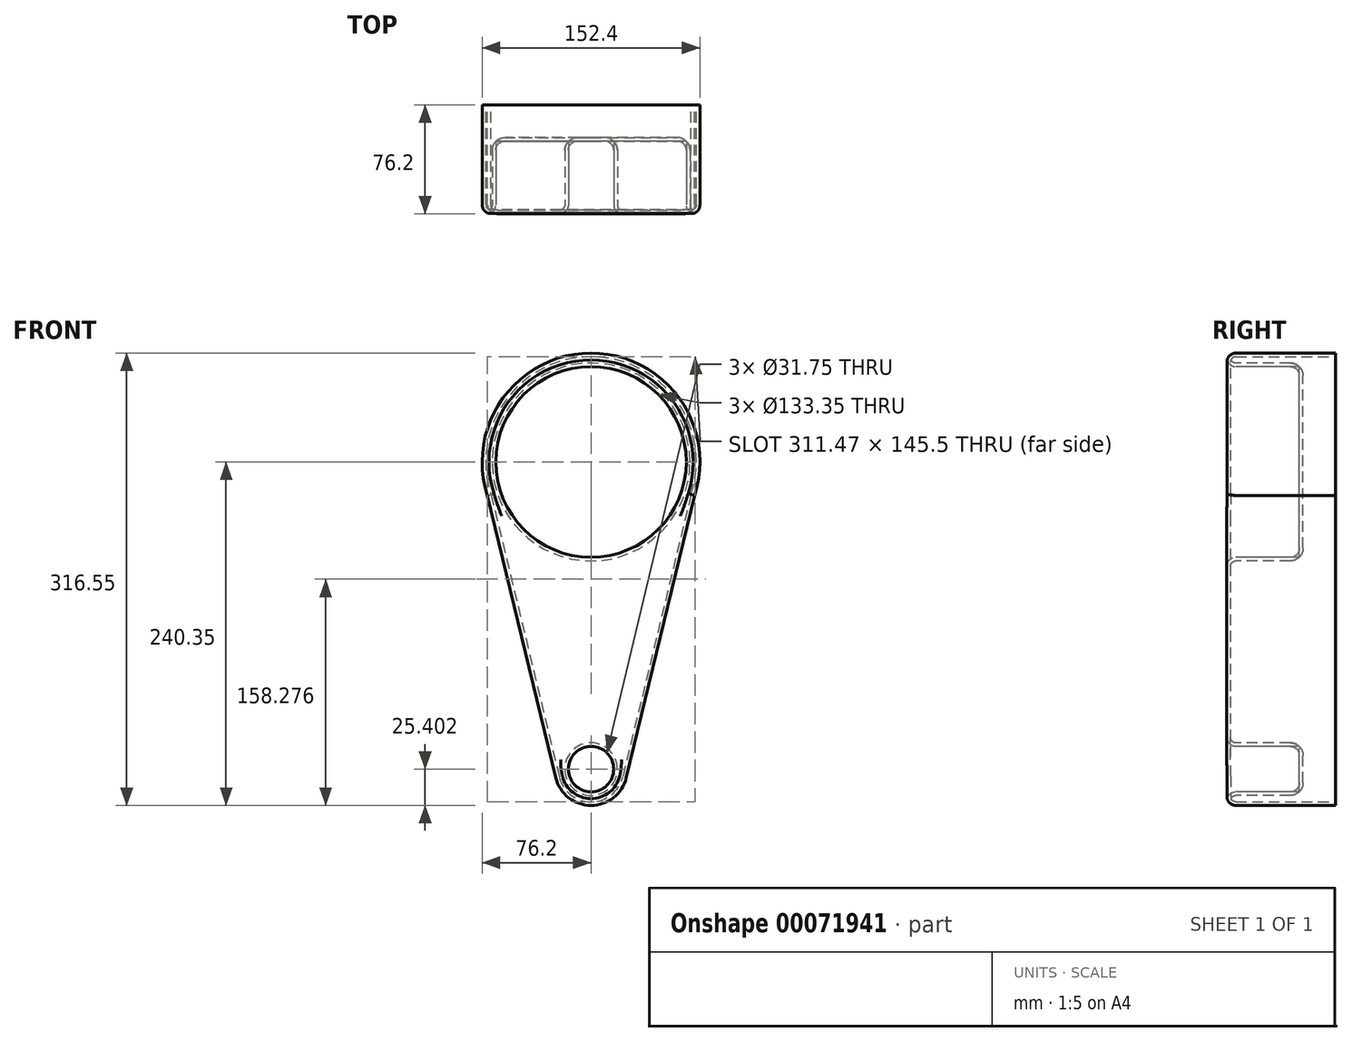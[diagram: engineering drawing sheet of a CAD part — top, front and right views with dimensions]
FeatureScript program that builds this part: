
annotation { "Feature Type Name" : "Feature", "Feature Type Description" : "" }
export const myFeature = defineFeature(function(context is Context, id is Id, definition is map)
    precondition{}
    {
        {
            var Q0;
            Q0=qCreatedBy(makeId("Front.planeOp"),FACE);
            var sketch = newSketch(context, id + "F0", { "sketchPlane" : qUnion([Q0])});
            skCircle(sketch, "E0", {"center": v(0, 0) * mm, "radius": 76.2 * mm});
            skCircle(sketch, "E1", {"center": v(0, -214.95) * mm, "radius": 25.4 * mm});
            skLineSegment(sketch, "E2", {"start": v(72.5, -23.43) * mm, "end": v(24.69, -220.93) * mm});
            skLineSegment(sketch, "E3", {"start": v(-72.5, -23.43) * mm, "end": v(-24.69, -220.93) * mm});
            skSolve(sketch);
        }
        {
            var Q0;
            Q0 = qSketchRegion(id + "F0", true);
            extrude(context, id + "F1", {"entities" : qUnion([Q0]), "depth" : 76.2 * mm});
        }
        {
            var Q0;
            Q0=makeQuery(id+"F1.opExtrude","CAP_FACE",FACE,{"disambiguationData":[OSD([sQuery(id+"F0.wireOp",EDGE,"E0"),sQuery(id+"F0.wireOp",EDGE,"E1"),sQuery(id+"F0.wireOp",EDGE,"E2"),sQuery(id+"F0.wireOp",EDGE,"E3")])],"isStart":false});
            var sketch = newSketch(context, id + "F2", { "sketchPlane" : qUnion([Q0])});
            skCircle(sketch, "E4", {"center": v(0, -214.95) * mm, "radius": 15.88 * mm});
            skCircle(sketch, "E5", {"center": v(0, 0) * mm, "radius": 66.68 * mm});
            skSolve(sketch);
        }
        {
            var Q0;
            Q0=makeQuery(id+"F2.imprint","IMPRINT",FACE,{"disambiguationData":[TD([[makeQuery(id+"F2.imprint","IMPRINT",EDGE,{"derivedFrom":sQuery(id+"F2.wireOp",EDGE,"E5")}),1.0]])]});
            var Q1;
            Q1=makeQuery(id+"F2.imprint","IMPRINT",FACE,{"disambiguationData":[TD([[makeQuery(id+"F2.imprint","IMPRINT",EDGE,{"derivedFrom":sQuery(id+"F2.wireOp",EDGE,"E4")}),1.0]])]});
            extrude(context, id + "F3", {"entities" : qUnion([Q0, Q1]), "operationType" : NewBodyOperationType.REMOVE, "oppositeDirection" : true, "depth" : 50.8 * mm});
        }
        {
            var Q0;
            Q0=makeQuery(id+"F1.opExtrude","CAP_FACE",FACE,{"disambiguationData":[OSD([sQuery(id+"F0.wireOp",EDGE,"E0"),sQuery(id+"F0.wireOp",EDGE,"E1"),sQuery(id+"F0.wireOp",EDGE,"E2"),sQuery(id+"F0.wireOp",EDGE,"E3")])],"isStart":false});
            var Q1;
            Q1=makeQuery(id+"F3.boolean.opBoolean","COPY",EDGE,{"derivedFrom":makeQuery(id+"F3.opExtrude","CAP_EDGE",EDGE,{"disambiguationData":[OSD([sQuery(id+"F2.wireOp",EDGE,"E4")])],"isStart":false})});
            var Q2;
            Q2=makeQuery(id+"F3.boolean.opBoolean","COPY",FACE,{"derivedFrom":makeQuery(id+"F3.opExtrude","SWEPT_FACE",FACE,{"disambiguationData":[OSD([sQuery(id+"F2.wireOp",EDGE,"E4")])]})});
            var Q3;
            Q3=makeQuery(id+"F3.boolean.opBoolean","COPY",FACE,{"derivedFrom":makeQuery(id+"F3.opExtrude","CAP_FACE",FACE,{"disambiguationData":[OSD([sQuery(id+"F2.wireOp",EDGE,"E5")])],"isStart":false})});
            fillet(context, id + "F4", {"entities" : qUnion([Q0, Q1, Q2, Q3]), "radius" : 6.35 * mm, "tangentPropagation" : true, "allowEdgeOverflow" : false});
        }
        {
            var Q0;
            Q0=makeQuery(id+"F1.opExtrude","CAP_FACE",FACE,{"disambiguationData":[OSD([sQuery(id+"F0.wireOp",EDGE,"E0"),sQuery(id+"F0.wireOp",EDGE,"E1"),sQuery(id+"F0.wireOp",EDGE,"E2"),sQuery(id+"F0.wireOp",EDGE,"E3")])],"isStart":true});
            shell(context, id + "F5", {"entities" : qUnion([Q0]), "thickness" : 2.54 * mm});
        }
    });
